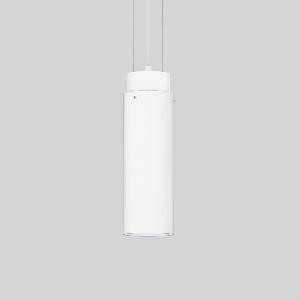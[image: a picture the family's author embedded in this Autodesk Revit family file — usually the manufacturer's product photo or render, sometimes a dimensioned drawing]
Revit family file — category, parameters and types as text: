
# Revit family: glasdownlight_931184_002_76_8e50
name_source: partatom
category: Lighting Fixtures
units: mm (PartAtom-declared; Revit-internal decimal feet)

## family parameters
Cut with Voids When Loaded = No
Host = Face
Light Source = No
Part Type = Normal
Room Calculation Point = No
Round Connector Dimension = Use Diameter
Shared = No

## types (1)
- GLASDOWNLIGHT (1 x LED Modul 830, 3350 lm, 3000)
    Apparent Load = 26 VA
    CIE Flux Codes = 24 49 74 56 100
    Color Rendering = 80
    Color Temperature = 3000
    Default Elevation = 1800 mm
    Description = Series: GLASDOWNLIGHT
Decorative round LED pendant luminaire. Canopy made of aluminium, powder-coated. Base: aluminium, powder-coated. Opal glass: mouth-blown, satin finish. Glass fastening: retaining screws. Suitable for pendant. 3-point steel cable suspension, steplessly adjustable. Special lengths available on request. 
Colour: white
Diameter: 150 mm
Height: 470 mm
Suspension length: 500-1250 mm
Lamp: LED
Socket: without socket
Colour temperature: 3000K
Colour rendering index (CRI): 80
System power: 26 W
Rated luminous flux: 3350 lm
Luminous efficiency: 129 lm/W
Control gear: Converter, dimmable, DALI
Protection class: I
Type of protection: IP 20
    Height = 470 mm
    Lamp = 1 x LED Modul 830
    Lamp Light Flux = 3350 lm
    Lamp count = 1
    Length = 150 mm
    Lifetime = 50000 h
    Luminous efficacy = 129 lm/W
    Manufacturer = RZB
    ModVariant = No
    Model = 931184.002.76
    Mounting Place = Ceiling
    Mounting Type = Pendant
    Number of Poles = 1
    OnlyDefault = Yes
    Power Factor = 1
    Product Name = GLASDOWNLIGHT
    Product group = Pendant luminaires
    ProductGroupID = 902
    Protection Class = Protection class I
    Protection Degree = Degree of protection
    RLX_Detail_Level = 1
    RLX_Emergency_Light_Flux = 0 lm
    RLX_Emergency_Type = 0
    RLX_Emergency_Type_DB = No
    RlxData = <blob elided: 13673 chars, md5=b2578da8>
    Socket = socket
    Standby Power = 0 W
    System Light Flux = 3350 lm
    System Power = 26 W
    Type Comments = Product without accessories
    Type Image = 931184.002.jpg
    URL = http://relux.com
    VarID = ---
    Voltage = 0 V
    Weight = 0.00 kg
    Width = 0 mm  [stored 0 ft]

note: [stored X ft] marks values corroborated as IEEE doubles in the binary element streams (Revit-internal decimal feet)

## geometry (parser evidence)
native form markers: Sweep x12
no freeform markers — native parametric forms only
